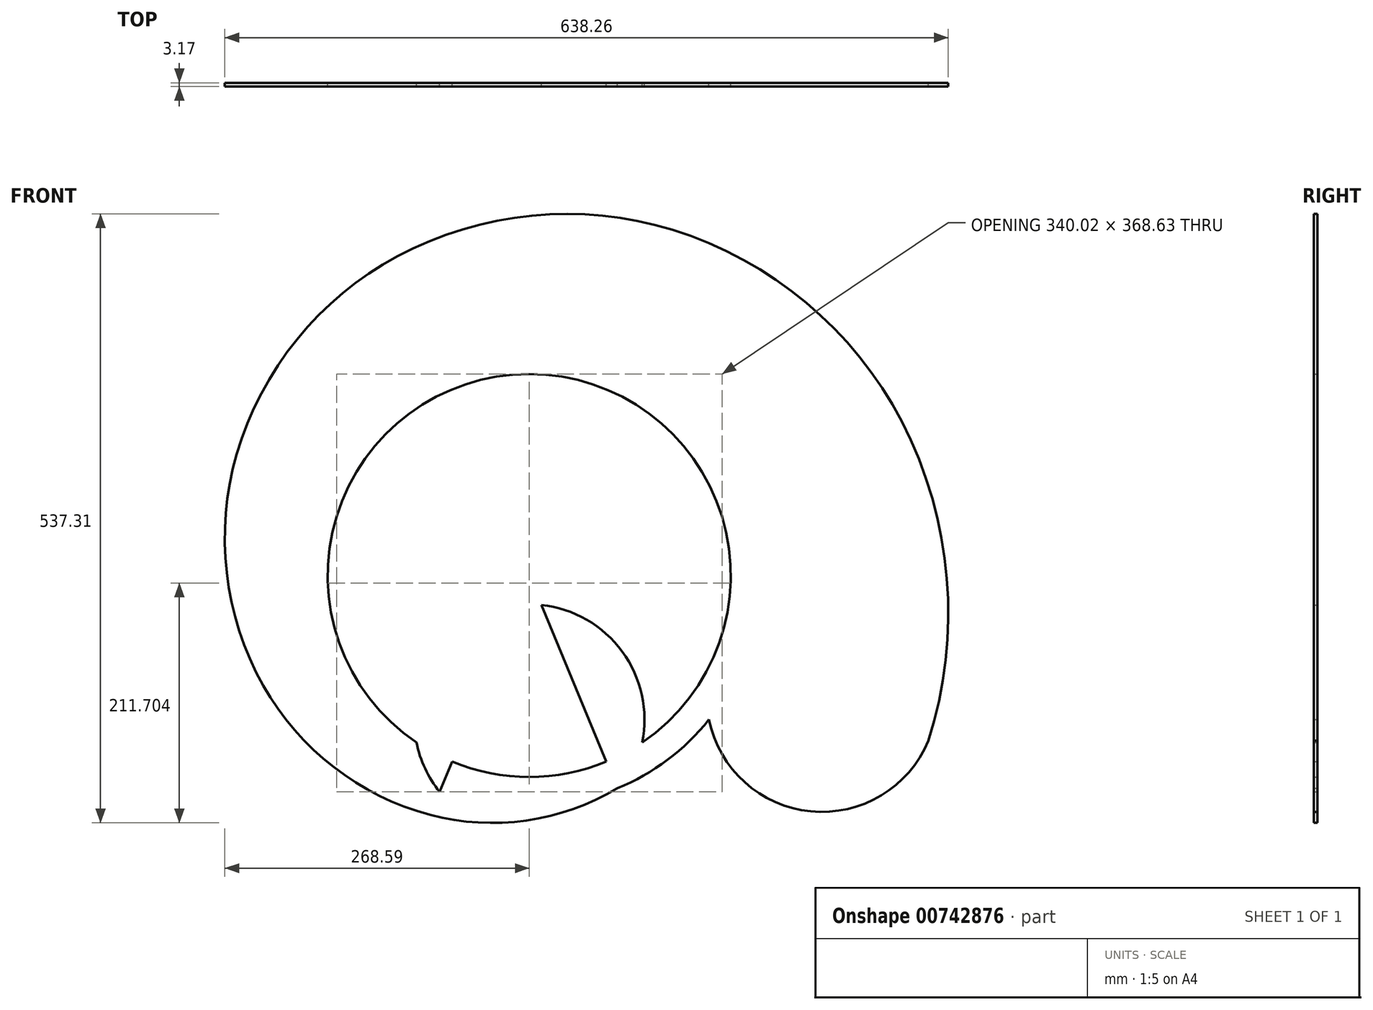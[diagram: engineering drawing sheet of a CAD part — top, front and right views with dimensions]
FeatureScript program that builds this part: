
annotation { "Feature Type Name" : "Feature", "Feature Type Description" : "" }
export const myFeature = defineFeature(function(context is Context, id is Id, definition is map)
    precondition{}
    {
        {
            var Q0;
            Q0=qCreatedBy(makeId("Front.planeOp"),FACE);
            var sketch = newSketch(context, id + "F0", { "sketchPlane" : qUnion([Q0])});
            skCircle(sketch, "E0", {"center": v(0, 0) * mm, "radius": 177.8 * mm});
            skLineSegment(sketch, "E1.4.0", {"start": v(0, 0) * mm, "end": v(0, -177.8) * mm});
            skLineSegment(sketch, "E2", {"start": v(0, 0) * mm, "end": v(0, -127) * mm});
            skCircle(sketch, "E3", {"center": v(0, -127) * mm, "radius": 101.6 * mm});
            skLineSegment(sketch, "E4", {"start": v(0, 0) * mm, "end": v(164.27, -68.04) * mm});
            skLineSegment(sketch, "E5", {"start": v(164.27, -68.04) * mm, "end": v(258.13, -106.92) * mm});
            skCircle(sketch, "E6", {"center": v(258.13, -106.92) * mm, "radius": 101.6 * mm});
            skLineSegment(sketch, "E7.1.0", {"start": v(0, 0) * mm, "end": v(164.27, 68.04) * mm});
            skLineSegment(sketch, "E7.2.0", {"start": v(0, 0) * mm, "end": v(68.04, 164.27) * mm});
            skLineSegment(sketch, "E7.3.0", {"start": v(0, 0) * mm, "end": v(-68.04, 164.27) * mm});
            skLineSegment(sketch, "E7.4.0", {"start": v(0, 0) * mm, "end": v(-164.27, 68.04) * mm});
            skLineSegment(sketch, "E7.5.0", {"start": v(0, 0) * mm, "end": v(-164.27, -68.04) * mm});
            skLineSegment(sketch, "E7.6.0", {"start": v(0, 0) * mm, "end": v(-68.04, -164.27) * mm});
            skLineSegment(sketch, "E7.7.0", {"start": v(0, 0) * mm, "end": v(68.04, -164.27) * mm});
            skLineSegment(sketch, "E8", {"start": v(164.27, 68.04) * mm, "end": v(328.53, 136.08) * mm});
            skLineSegment(sketch, "E9", {"start": v(68.04, 164.27) * mm, "end": v(126.36, 305.07) * mm});
            skLineSegment(sketch, "E10", {"start": v(-68.04, 164.27) * mm, "end": v(-116.64, 281.6) * mm});
            skLineSegment(sketch, "E11", {"start": v(-164.27, 68.04) * mm, "end": v(-258.13, 106.92) * mm});
            skLineSegment(sketch, "E12", {"start": v(-164.27, -68.04) * mm, "end": v(-234.67, -97.2) * mm});
            skLineSegment(sketch, "E13", {"start": v(164.27, -68.04) * mm, "end": v(352, -145.8) * mm});
            skLineSegment(sketch, "E14", {"start": v(-68.04, -164.27) * mm, "end": v(-87.48, -211.2) * mm});
            skLineSegment(sketch, "E15", {"start": v(68.04, -164.27) * mm, "end": v(77.76, -187.73) * mm});
            skArc(sketch, "E16", {"start": v(352, -145.8) * mm, "mid": v(368.4, -2.52) * mm, "end": v(328.53, 136.08) * mm});
            skArc(sketch, "E17", {"start": v(328.53, 136.08) * mm, "mid": v(244.33, 240.77) * mm, "end": v(126.36, 305.07) * mm});
            skArc(sketch, "E18", {"start": v(126.36, 305.07) * mm, "mid": v(2.51, 317.62) * mm, "end": v(-116.64, 281.6) * mm});
            skArc(sketch, "E19", {"start": v(-116.64, 281.6) * mm, "mid": v(-204.86, 208.42) * mm, "end": v(-258.13, 106.92) * mm});
            skArc(sketch, "E20", {"start": v(-258.13, 106.92) * mm, "mid": v(-266.84, 2.5) * mm, "end": v(-234.67, -97.2) * mm});
            skArc(sketch, "E21", {"start": v(-234.67, -97.2) * mm, "mid": v(-172.5, -168.97) * mm, "end": v(-87.48, -211.2) * mm});
            skArc(sketch, "E22", {"start": v(-87.48, -211.2) * mm, "mid": v(-2.5, -216.08) * mm, "end": v(77.76, -187.73) * mm});
            skArc(sketch, "E23", {"start": v(77.76, -187.73) * mm, "mid": v(121.99, -162.51) * mm, "end": v(158.55, -127.09) * mm});
            skSolve(sketch);
        }
        {
            var Q0;
            {var subQ0=sQuery(id+"F0.wireOp",EDGE,"E10");Q0=makeQuery(id+"F0.imprint","IMPRINT",FACE,{"disambiguationData":[TD([[makeQuery(id+"F0.imprint","IMPRINT",EDGE,{"derivedFrom":subQ0}),1.0]])]});}
            var Q1;
            {var subQ0=sQuery(id+"F0.wireOp",EDGE,"E9");Q1=makeQuery(id+"F0.imprint","IMPRINT",FACE,{"disambiguationData":[TD([[makeQuery(id+"F0.imprint","IMPRINT",EDGE,{"derivedFrom":subQ0}),1.0]])]});}
            var Q2;
            {var subQ0=sQuery(id+"F0.wireOp",EDGE,"E8");Q2=makeQuery(id+"F0.imprint","IMPRINT",FACE,{"disambiguationData":[TD([[makeQuery(id+"F0.imprint","IMPRINT",EDGE,{"derivedFrom":subQ0}),1.0]])]});}
            var Q3;
            {var subQ3=sQuery(id+"F0.wireOp",EDGE,"E8");Q3=makeQuery(id+"F0.imprint","IMPRINT",FACE,{"disambiguationData":[TD([[makeQuery(id+"F0.imprint","IMPRINT",EDGE,{"derivedFrom":subQ3}),-1.0]])]});}
            var Q4;
            {var subQ0=sQuery(id+"F0.wireOp",EDGE,"E13");var subQ5=makeQuery(id+"F0.imprint","IMPRINT",VERTEX,{"derivedFrom":subQ0});Q4=makeQuery(id+"F0.imprint","IMPRINT",FACE,{"disambiguationData":[TD([[makeQuery(id+"F0.imprint","IMPRINT",EDGE,{"disambiguationData":[TD([[subQ5,-1.0]])],"derivedFrom":subQ0}),1.0]])]});}
            var Q5;
            {var subQ0=sQuery(id+"F0.wireOp",EDGE,"E13");var subQ5=makeQuery(id+"F0.imprint","IMPRINT",VERTEX,{"derivedFrom":subQ0});Q5=makeQuery(id+"F0.imprint","IMPRINT",FACE,{"disambiguationData":[TD([[makeQuery(id+"F0.imprint","IMPRINT",EDGE,{"disambiguationData":[TD([[subQ5,-1.0]])],"derivedFrom":subQ0}),-1.0]])]});}
            var Q6;
            {var subQ3=sQuery(id+"F0.wireOp",EDGE,"E3");var subQ5=sQuery(id+"F0.wireOp",EDGE,"E23");var subQ6=makeQuery(id+"F0.imprint","INTERSECT",VERTEX,{"derivedFrom":[subQ3,subQ5]});Q6=makeQuery(id+"F0.imprint","IMPRINT",FACE,{"disambiguationData":[TD([[makeQuery(id+"F0.imprint","IMPRINT",EDGE,{"disambiguationData":[TD([[subQ6,-1.0]])],"derivedFrom":subQ3}),-1.0]])]});}
            var Q7;
            {var subQ0=sQuery(id+"F0.wireOp",EDGE,"E15");Q7=makeQuery(id+"F0.imprint","IMPRINT",FACE,{"disambiguationData":[TD([[makeQuery(id+"F0.imprint","IMPRINT",EDGE,{"derivedFrom":subQ0}),1.0]])]});}
            var Q8;
            {var subQ6=sQuery(id+"F0.wireOp",EDGE,"E15");Q8=makeQuery(id+"F0.imprint","IMPRINT",FACE,{"disambiguationData":[TD([[makeQuery(id+"F0.imprint","IMPRINT",EDGE,{"derivedFrom":subQ6}),-1.0]])]});}
            var Q9;
            {var subQ0=sQuery(id+"F0.wireOp",EDGE,"E22");var subQ1=sQuery(id+"F0.wireOp",EDGE,"E3");var subQ2=makeQuery(id+"F0.imprint","INTERSECT",VERTEX,{"derivedFrom":[subQ1,subQ0]});Q9=makeQuery(id+"F0.imprint","IMPRINT",FACE,{"disambiguationData":[TD([[makeQuery(id+"F0.imprint","IMPRINT",EDGE,{"disambiguationData":[TD([[subQ2,1.0]])],"derivedFrom":subQ1}),-1.0]])]});}
            var Q10;
            {var subQ0=sQuery(id+"F0.wireOp",EDGE,"E12");Q10=makeQuery(id+"F0.imprint","IMPRINT",FACE,{"disambiguationData":[TD([[makeQuery(id+"F0.imprint","IMPRINT",EDGE,{"derivedFrom":subQ0}),1.0]])]});}
            var Q11;
            {var subQ1=sQuery(id+"F0.wireOp",EDGE,"E0");var subQ3=sQuery(id+"F0.wireOp",EDGE,"E3");var subQ4=makeQuery(id+"F0.imprint","INTERSECT",VERTEX,{"disambiguationData":[OD(0.0)],"derivedFrom":[subQ1,subQ3]});Q11=makeQuery(id+"F0.imprint","IMPRINT",FACE,{"disambiguationData":[TD([[makeQuery(id+"F0.imprint","IMPRINT",EDGE,{"disambiguationData":[TD([[subQ4,-1.0]])],"derivedFrom":subQ3}),1.0]])]});}
            var Q12;
            {var subQ0=sQuery(id+"F0.wireOp",EDGE,"E11");Q12=makeQuery(id+"F0.imprint","IMPRINT",FACE,{"disambiguationData":[TD([[makeQuery(id+"F0.imprint","IMPRINT",EDGE,{"derivedFrom":subQ0}),1.0]])]});}
            extrude(context, id + "F1", {"entities" : qUnion([Q0, Q1, Q2, Q3, Q4, Q5, Q6, Q7, Q8, Q9, Q10, Q11, Q12]), "depth" : 3.17 * mm, "offsetDistance" : 25.4 * mm});
        }
    });
